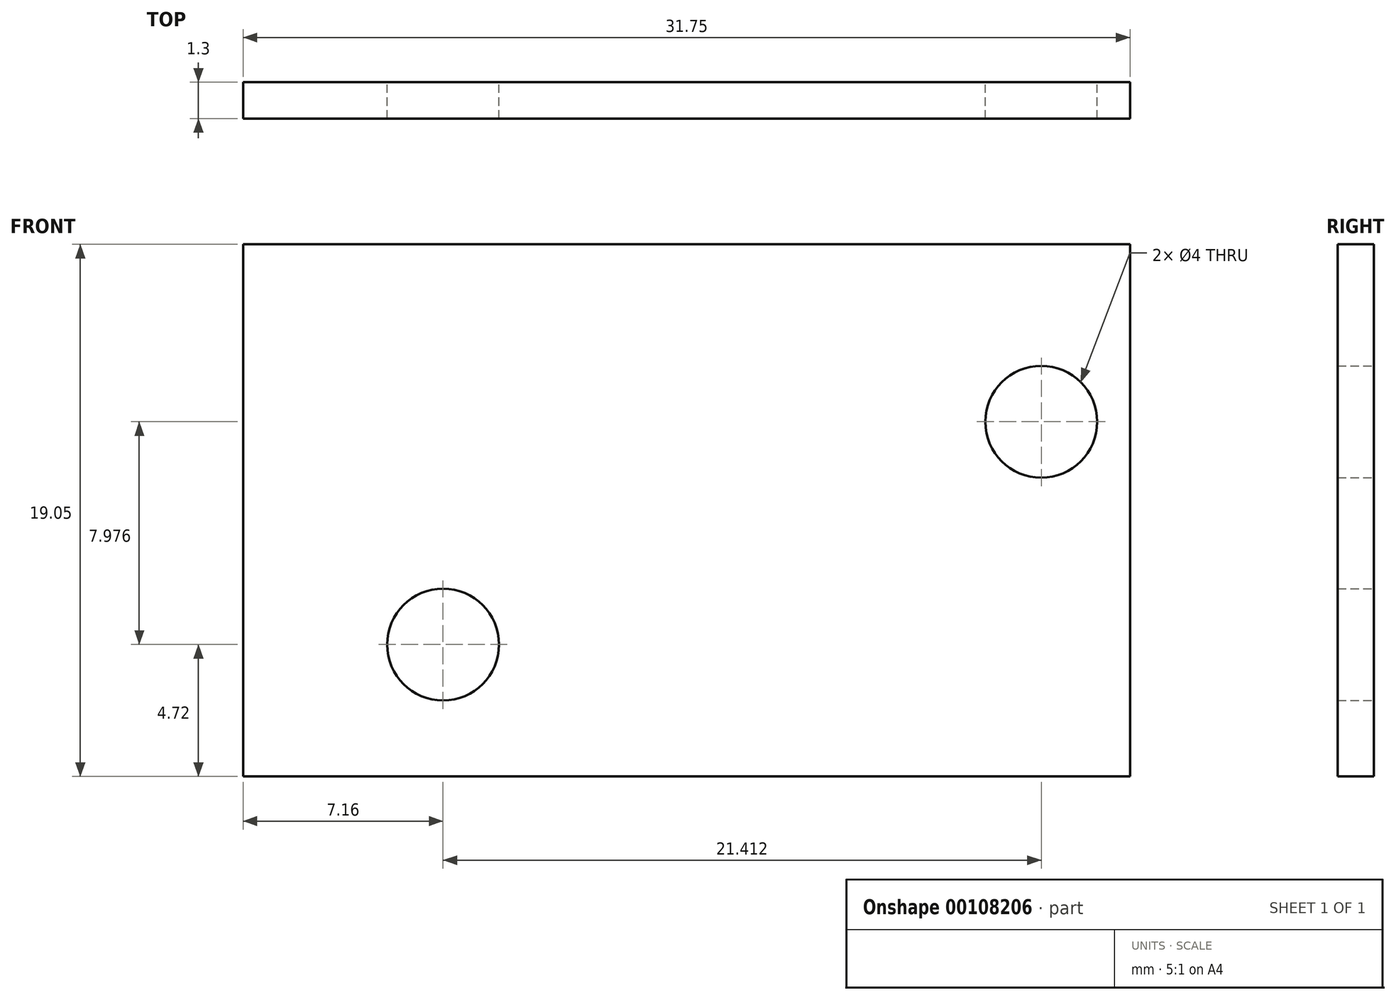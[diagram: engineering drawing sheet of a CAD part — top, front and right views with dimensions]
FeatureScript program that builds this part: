
annotation { "Feature Type Name" : "Feature", "Feature Type Description" : "" }
export const myFeature = defineFeature(function(context is Context, id is Id, definition is map)
    precondition{}
    {
        {
            var Q0;
            Q0=qCreatedBy(makeId("Front.planeOp"),FACE);
            var sketch = newSketch(context, id + "F0", { "sketchPlane" : qUnion([Q0])});
            skCircle(sketch, "E0", {"center": v(0, 0) * mm, "radius": 2 * mm});
            skCircle(sketch, "E1", {"center": v(21.41, 7.98) * mm, "radius": 2 * mm});
            skLineSegment(sketch, "E2.bottom", {"start": v(-7.16, -4.72) * mm, "end": v(24.59, -4.72) * mm});
            skLineSegment(sketch, "E2.top", {"start": v(-7.16, 14.33) * mm, "end": v(24.59, 14.33) * mm});
            skLineSegment(sketch, "E2.left", {"start": v(-7.16, -4.72) * mm, "end": v(-7.16, 14.33) * mm});
            skLineSegment(sketch, "E2.right", {"start": v(24.59, -4.72) * mm, "end": v(24.59, 14.33) * mm});
            skSolve(sketch);
        }
        {
            var Q0;
            Q0 = qSketchRegion(id + "F0", true);
            extrude(context, id + "F1", {"entities" : qUnion([Q0]), "depth" : 1.3 * mm});
        }
    });
